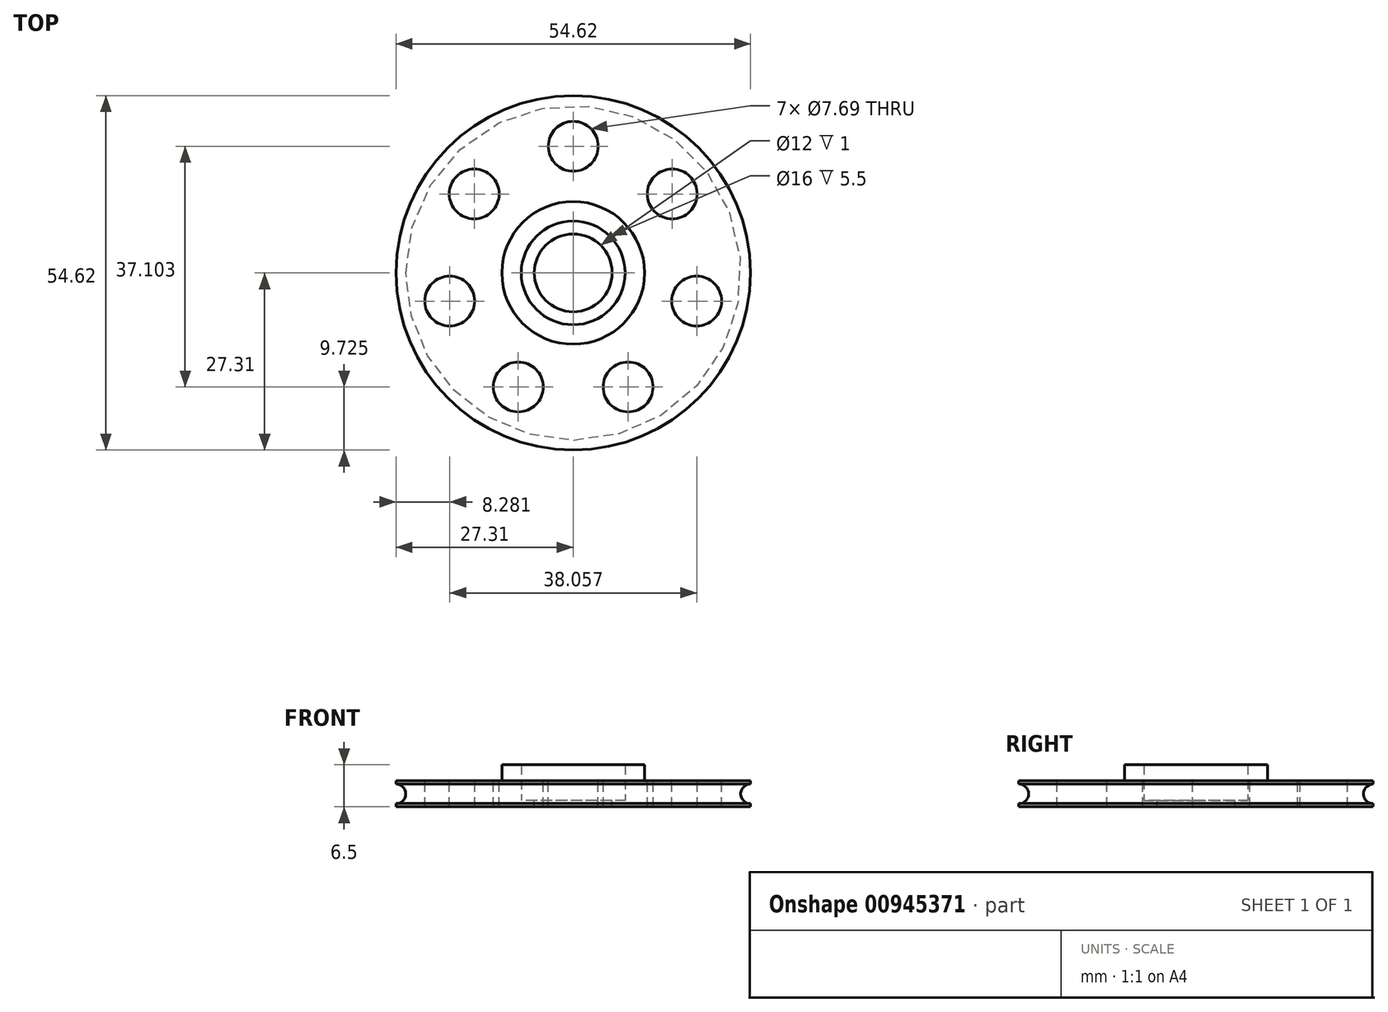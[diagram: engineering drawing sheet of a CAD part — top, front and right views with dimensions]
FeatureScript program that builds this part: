
annotation { "Feature Type Name" : "Feature", "Feature Type Description" : "" }
export const myFeature = defineFeature(function(context is Context, id is Id, definition is map)
    precondition{}
    {
        {
            var Q0;
            Q0=qCreatedBy(makeId("Top.planeOp"),FACE);
            var sketch = newSketch(context, id + "F0", { "sketchPlane" : qUnion([Q0])});
            skCircle(sketch, "E0", {"center": v(0, 0) * mm, "radius": 27.3 * mm});
            skSolve(sketch);
        }
        {
            var Q0;
            Q0=makeQuery(id+"F0.imprint","IMPRINT",FACE,{"disambiguationData":[TD([[makeQuery(id+"F0.imprint","IMPRINT",EDGE,{"derivedFrom":sQuery(id+"F0.wireOp",EDGE,"E0")}),1.0]])]});
            extrude(context, id + "F1", {"entities" : qUnion([Q0]), "depth" : 4 * mm, "offsetDistance" : 25.4 * mm});
        }
        {
            var Q0;
            Q0=makeQuery(id+"F1.opExtrude","CAP_FACE",FACE,{"disambiguationData":[OSD([sQuery(id+"F0.wireOp",EDGE,"E0"),sQuery(id+"F0.wireOp",EDGE,"n39IqKt5-bk1q-LU1x-fgod-8OyBNiFTd7FZ")])],"isStart":false});
            var sketch = newSketch(context, id + "F2", { "sketchPlane" : qUnion([Q0])});
            skCircle(sketch, "E1", {"center": v(0, 0) * mm, "radius": 8 * mm});
            skCircle(sketch, "E2.0", {"center": v(0, 0) * mm, "radius": 11 * mm});
            skSolve(sketch);
        }
        {
            var Q0;
            Q0=qSketchRegion(id+"F2",true);
            extrude(context, id + "F3", {"entities" : qUnion([Q0]), "operationType" : NewBodyOperationType.ADD, "flatOperationType" : FlatOperationType.REMOVE, "depth" : 2.5 * mm, "offsetDistance" : 25.4 * mm, "domain" : OperationDomain.MODEL});
        }
        {
            var Q0;
            Q0=makeQuery(id+"F3.boolean.opBoolean","SPLIT",FACE,{"disambiguationData":[TD([makeQuery(id+"F3.opExtrude","SWEPT_FACE",FACE,{"disambiguationData":[OSD([sQuery(id+"F2.wireOp",EDGE,"E1")])]})])],"derivedFrom":makeQuery(id+"F1.opExtrude","CAP_FACE",FACE,{"disambiguationData":[OSD([sQuery(id+"F0.wireOp",EDGE,"E0")])],"isStart":false})});
            var sketch = newSketch(context, id + "F4", { "sketchPlane" : qUnion([Q0])});
            skCircle(sketch, "E3", {"center": v(0, 0) * mm, "radius": 6 * mm});
            skSolve(sketch);
        }
        {
            var Q0;
            Q0=makeQuery(id+"F4.imprint","IMPRINT",FACE,{"disambiguationData":[TD([[makeQuery(id+"F4.imprint","IMPRINT",EDGE,{"derivedFrom":sQuery(id+"F4.wireOp",EDGE,"E3")}),1.0]])]});
            var Q1;
            Q1=makeQuery(id+"F4.imprint","IMPRINT",FACE,{"disambiguationData":[TD([[makeQuery(id+"F4.imprint","IMPRINT",EDGE,{"derivedFrom":makeQuery(id+"FgYK8jIepfClWtA_1.opExtrude","CAP_EDGE",EDGE,{"disambiguationData":[OSD([sQuery(id+"F8DXjnVyigKkjng_1.wireOp",EDGE,"EUjAMsCd-Zx2B-3j4q-cP5o-T3GrjTijNDqK")])],"isStart":false})}),1.0]])]});
            extrude(context, id + "F5", {"entities" : qUnion([Q0, Q1]), "operationType" : NewBodyOperationType.REMOVE, "oppositeDirection" : true, "depth" : 9 * mm, "offsetDistance" : 25.4 * mm});
        }
        {
            var Q0;
            Q0=qCreatedBy(makeId("Front.planeOp"),FACE);
            var sketch = newSketch(context, id + "F6", { "sketchPlane" : qUnion([Q0])});
            skCircle(sketch, "E4", {"center": v(-27.3, 2) * mm, "radius": 1.5 * mm});
            skLineSegment(sketch, "E5.bottom", {"start": v(-25.8, 0.65) * mm, "end": v(-27.95, 0.65) * mm});
            skLineSegment(sketch, "E5.top", {"start": v(-25.8, 3.35) * mm, "end": v(-27.95, 3.35) * mm});
            skLineSegment(sketch, "E5.left", {"start": v(-25.8, 0.65) * mm, "end": v(-25.8, 3.35) * mm});
            skLineSegment(sketch, "E5.right", {"start": v(-28.8, 1.91) * mm, "end": v(-28.8, 2.09) * mm});
            skLineSegment(sketch, "E6", {"start": v(0, 19.1) * mm, "end": v(0, -12.61) * mm, "construction": true});
            skLineSegment(sketch, "E7", {"start": v(-25.8, 1.83) * mm, "end": v(-25.81, 1.83) * mm});
            skPoint(sketch, "E8.orphan", {"position": v(-38.97, 3.35) * mm});
            skPoint(sketch, "E9.end.orphan", {"position": v(-15.64, 0.65) * mm});
            skPoint(sketch, "E9.start.orphan", {"position": v(-25.8, 2) * mm});
            skSolve(sketch);
        }
        {
            var Q0;
            {var subQ0=sQuery(id+"F6.wireOp",EDGE,"E5.top");var subQ1=sQuery(id+"F6.wireOp",EDGE,"E4");var subQ2=makeQuery(id+"F6.imprint","INTERSECT",VERTEX,{"disambiguationData":[OD(0.0)],"derivedFrom":[subQ1,subQ0]});Q0=makeQuery(id+"F6.imprint","IMPRINT",FACE,{"disambiguationData":[TD([[makeQuery(id+"F6.imprint","IMPRINT",EDGE,{"disambiguationData":[TD([[subQ2,1.0]])],"derivedFrom":subQ1}),1.0]])]});}
            var Q1;
            {var subQ0=sQuery(id+"F6.wireOp",EDGE,"E5.bottom");var subQ1=sQuery(id+"F6.wireOp",EDGE,"E4");var subQ2=makeQuery(id+"F6.imprint","INTERSECT",VERTEX,{"disambiguationData":[OD(0.0)],"derivedFrom":[subQ1,subQ0]});Q1=makeQuery(id+"F6.imprint","IMPRINT",FACE,{"disambiguationData":[TD([[makeQuery(id+"F6.imprint","IMPRINT",EDGE,{"disambiguationData":[TD([[subQ2,-1.0]])],"derivedFrom":subQ1}),1.0]])]});}
            var Q2;
            {var subQ4=sQuery(id+"F6.wireOp",EDGE,"E5.right");Q2=makeQuery(id+"F6.imprint","IMPRINT",FACE,{"disambiguationData":[TD([[makeQuery(id+"F6.imprint","IMPRINT",EDGE,{"derivedFrom":subQ4}),-1.0]])]});}
            var Q3;
            {var subQ0=sQuery(id+"F6.wireOp",EDGE,"p3G3spWP-JurA-dj01-Cwvm-HHlCDoPDIoxd");Q3=makeQuery(id+"F6.imprint","IMPRINT",FACE,{"disambiguationData":[TD([[makeQuery(id+"F6.imprint","IMPRINT",EDGE,{"derivedFrom":subQ0}),1.0]])]});}
            var Q4;
            Q4=makeQuery(id+"F6.imprint","IMPRINT",FACE,{"disambiguationData":[TD([[makeQuery(id+"F6.imprint","IMPRINT",EDGE,{"derivedFrom":sQuery(id+"F6.wireOp",EDGE,"p3G3spWP-JurA-dj01-Cwvm-HHlCDoPDIoxd")}),-1.0]])]});
            var Q5;
            {var subQ0=sQuery(id+"F6.wireOp",EDGE,"E9");Q5=makeQuery(id+"F6.imprint","IMPRINT",FACE,{"disambiguationData":[TD([[makeQuery(id+"F6.imprint","IMPRINT",EDGE,{"derivedFrom":subQ0}),1.0]])]});}
            var Q6;
            Q6=sQuery(id+"F6.wireOp",EDGE,"E6");
            revolve(context, id + "F7", {"operationType" : NewBodyOperationType.REMOVE, "surfaceOperationType" : NewSurfaceOperationType.NEW, "entities" : qUnion([Q0, Q1, Q2, Q3, Q4, Q5]), "axis" : qUnion([Q6]), "revolveType" : RevolveType.FULL, "oppositeDirection" : true});
        }
        {
            var Q0;
            Q0=makeQuery(id+"F3.boolean.opBoolean","SPLIT",FACE,{"disambiguationData":[TD([makeQuery(id+"F3.opExtrude","SWEPT_FACE",FACE,{"disambiguationData":[OSD([sQuery(id+"F2.wireOp",EDGE,"E1")])]})])],"derivedFrom":makeQuery(id+"F1.opExtrude","CAP_FACE",FACE,{"disambiguationData":[OSD([sQuery(id+"F0.wireOp",EDGE,"E0")])],"isStart":false})});
            extrude(context, id + "F8", {"entities" : qUnion([Q0]), "operationType" : NewBodyOperationType.REMOVE, "oppositeDirection" : true, "depth" : 3 * mm, "offsetDistance" : 25 * mm});
        }
        {
            var Q0;
            {var subQ0=sQuery(id+"F0.wireOp",EDGE,"E0");var subQ1=makeQuery(id+"F1.opExtrude","SWEPT_FACE",FACE,{"disambiguationData":[OSD([subQ0])]});Q0=makeQuery(id+"FvaswZWDLJZ7FP9_1.boolean.opBoolean","SPLIT",FACE,{"disambiguationData":[TD([subQ1])],"derivedFrom":makeQuery(id+"F3.boolean.opBoolean","SPLIT",FACE,{"disambiguationData":[TD([subQ1])],"derivedFrom":makeQuery(id+"F1.opExtrude","CAP_FACE",FACE,{"disambiguationData":[OSD([subQ0])],"isStart":false})})});}
            var sketch = newSketch(context, id + "F9", { "sketchPlane" : qUnion([Q0])});
            skCircle(sketch, "E10", {"center": v(0, 19.52) * mm, "radius": 3.84 * mm});
            skCircle(sketch, "E11.1.0", {"center": v(-15.26, 12.17) * mm, "radius": 3.84 * mm});
            skCircle(sketch, "E11.2.0", {"center": v(-19.03, -4.34) * mm, "radius": 3.84 * mm});
            skCircle(sketch, "E11.3.0", {"center": v(-8.47, -17.58) * mm, "radius": 3.84 * mm});
            skCircle(sketch, "E11.4.0", {"center": v(8.47, -17.58) * mm, "radius": 3.84 * mm});
            skCircle(sketch, "E11.5.0", {"center": v(19.03, -4.34) * mm, "radius": 3.84 * mm});
            skCircle(sketch, "E11.6.0", {"center": v(15.26, 12.17) * mm, "radius": 3.84 * mm});
            skPoint(sketch, "E11.center", {"position": v(0, 0) * mm});
            skSolve(sketch);
        }
        {
            var Q0;
            Q0 = qSketchRegion(id + "F9", true);
            extrude(context, id + "F10", {"entities" : qUnion([Q0]), "operationType" : NewBodyOperationType.REMOVE, "oppositeDirection" : true, "depth" : 25 * mm, "offsetDistance" : 25 * mm});
        }
    });
